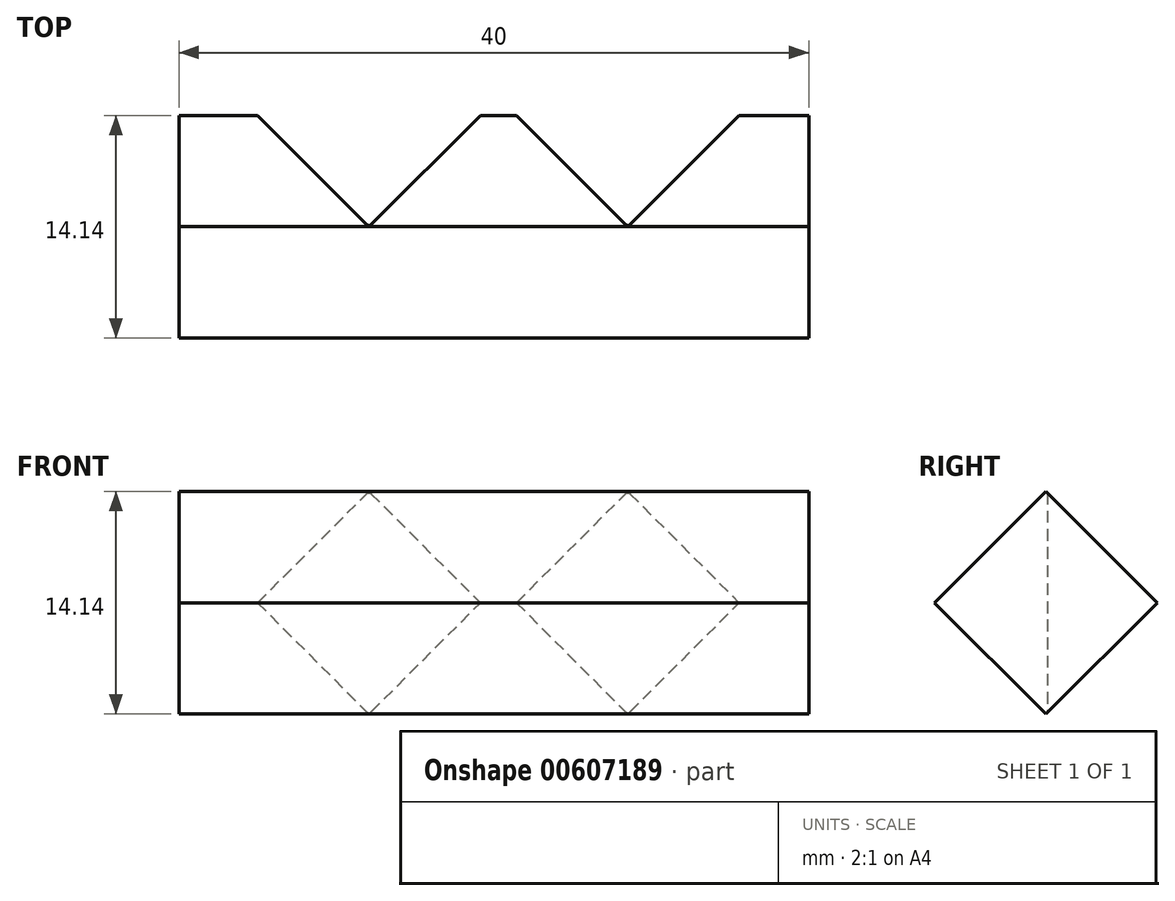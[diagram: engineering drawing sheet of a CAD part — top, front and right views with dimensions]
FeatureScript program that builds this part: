
annotation { "Feature Type Name" : "Feature", "Feature Type Description" : "" }
export const myFeature = defineFeature(function(context is Context, id is Id, definition is map)
    precondition{}
    {
        {
            var Q0;
            Q0=qCreatedBy(makeId("Top.planeOp"),FACE);
            var sketch = newSketch(context, id + "F0", { "sketchPlane" : qUnion([Q0])});
            skLineSegment(sketch, "E0.bottom", {"start": v(20, -5) * mm, "end": v(-20, -5) * mm});
            skLineSegment(sketch, "E0.top", {"start": v(20, 5) * mm, "end": v(-20, 5) * mm});
            skLineSegment(sketch, "E0.left", {"start": v(20, -5) * mm, "end": v(20, 5) * mm});
            skLineSegment(sketch, "E0.right", {"start": v(-20, -5) * mm, "end": v(-20, 5) * mm});
            skPoint(sketch, "E0.middle", {"position": v(0, 0) * mm});
            skLineSegment(sketch, "E1", {"start": v(20, 0) * mm, "end": v(-20, 0) * mm, "construction": true});
            skLineSegment(sketch, "E2", {"start": v(0, 5) * mm, "end": v(0, -5) * mm, "construction": true});
            skSolve(sketch);
        }
        {
            var Q0;
            Q0=makeQuery(id+"F0.imprint","IMPRINT",FACE,{"disambiguationData":[TD([[makeQuery(id+"F0.imprint","IMPRINT",EDGE,{"derivedFrom":sQuery(id+"F0.wireOp",EDGE,"E0.bottom")}),-1.0]])]});
            cPlane(context, id + "F1", {"entities" : qUnion([Q0]), "cplaneType" : CPlaneType.OFFSET, "offset" : 5 * mm, "width" : 150 * mm, "height" : 150 * mm});
        }
        {
            var Q0;
            Q0=makeQuery(id+"F0.imprint","IMPRINT",FACE,{"disambiguationData":[TD([[makeQuery(id+"F0.imprint","IMPRINT",EDGE,{"derivedFrom":sQuery(id+"F0.wireOp",EDGE,"E0.bottom")}),-1.0]])]});
            extrude(context, id + "F2", {"entities" : qUnion([Q0]), "endBound" : BoundingType.SYMMETRIC, "depth" : 10 * mm, "offsetDistance" : 25 * mm});
        }
        {
            var Q0;
            Q0=makeQuery(id+"F2.opExtrude","SWEPT_BODY",BODY,{"disambiguationData":[OSD([sQuery(id+"F0.wireOp",EDGE,"E0.bottom"),sQuery(id+"F0.wireOp",EDGE,"E0.top"),sQuery(id+"F0.wireOp",EDGE,"E0.left"),sQuery(id+"F0.wireOp",EDGE,"E0.right")])]});
            var Q1;
            Q1=sQuery(id+"F0.wireOp",EDGE,"E1");
            transform(context, id + "F3", {"entities" : qUnion([Q0]), "transformType" : TransformType.ROTATION, "transformAxis" : qUnion([Q1]), "angle" : 45 * degree, "makeCopy" : false});
        }
        {
            var Q0;
            Q0=qCreatedBy(id+"F1.planeOp",FACE);
            var sketch = newSketch(context, id + "F4", { "sketchPlane" : qUnion([Q0])});
            skLineSegment(sketch, "E3", {"start": v(-15, 7.07) * mm, "end": v(-7.93, 0) * mm});
            skLineSegment(sketch, "E4", {"start": v(-7.93, 0) * mm, "end": v(-0.86, 7.07) * mm});
            skLineSegment(sketch, "E5", {"start": v(-0.86, 7.07) * mm, "end": v(-15, 7.07) * mm});
            skLineSegment(sketch, "E6", {"start": v(1.44, 7.07) * mm, "end": v(8.51, 0) * mm});
            skLineSegment(sketch, "E7", {"start": v(8.51, 0) * mm, "end": v(15.58, 7.07) * mm});
            skLineSegment(sketch, "E8", {"start": v(15.58, 7.07) * mm, "end": v(1.44, 7.07) * mm});
            skSolve(sketch);
        }
        {
            var Q0;
            Q0=makeQuery(id+"F4.imprint","IMPRINT",FACE,{"disambiguationData":[TD([[makeQuery(id+"F4.imprint","IMPRINT",EDGE,{"derivedFrom":sQuery(id+"F4.wireOp",EDGE,"E3")}),1.0]])]});
            var Q1;
            Q1=makeQuery(id+"F4.imprint","IMPRINT",FACE,{"disambiguationData":[TD([[makeQuery(id+"F4.imprint","IMPRINT",EDGE,{"derivedFrom":sQuery(id+"F4.wireOp",EDGE,"4396284b-7444-46be-a8a5-f45a6c6d6953")}),1.0]])]});
            var Q2;
            Q2=makeQuery(id+"F4.imprint","IMPRINT",FACE,{"disambiguationData":[TD([[makeQuery(id+"F4.imprint","IMPRINT",EDGE,{"derivedFrom":sQuery(id+"F4.wireOp",EDGE,"E6")}),1.0]])]});
            extrude(context, id + "F5", {"entities" : qUnion([Q0, Q1, Q2]), "operationType" : NewBodyOperationType.REMOVE, "endBound" : BoundingType.SYMMETRIC, "oppositeDirection" : true, "depth" : 25 * mm, "offsetDistance" : 25 * mm});
        }
        {
            var Q0;
            Q0=makeQuery(id+"F5.boolean.opBoolean","COPY",EDGE,{"derivedFrom":makeQuery(id+"F5.opExtrude","SWEPT_EDGE",EDGE,{"disambiguationData":[OSD([sQuery(id+"F4.wireOp",EDGE,"E3"),sQuery(id+"F4.wireOp",EDGE,"E4")])]})});
            fillet(context, id + "F6", {"entities" : qUnion([Q0]), "radius" : 0.2 * mm, "tangentPropagation" : true, "allowEdgeOverflow" : false});
        }
        {
            var Q0;
            Q0=makeQuery(id+"F5.boolean.opBoolean","COPY",EDGE,{"derivedFrom":makeQuery(id+"F5.opExtrude","SWEPT_EDGE",EDGE,{"disambiguationData":[OSD([sQuery(id+"F4.wireOp",EDGE,"E6"),sQuery(id+"F4.wireOp",EDGE,"E7")])]})});
            fillet(context, id + "F7", {"entities" : qUnion([Q0]), "radius" : 0.2 * mm, "tangentPropagation" : true, "allowEdgeOverflow" : false});
        }
    });
